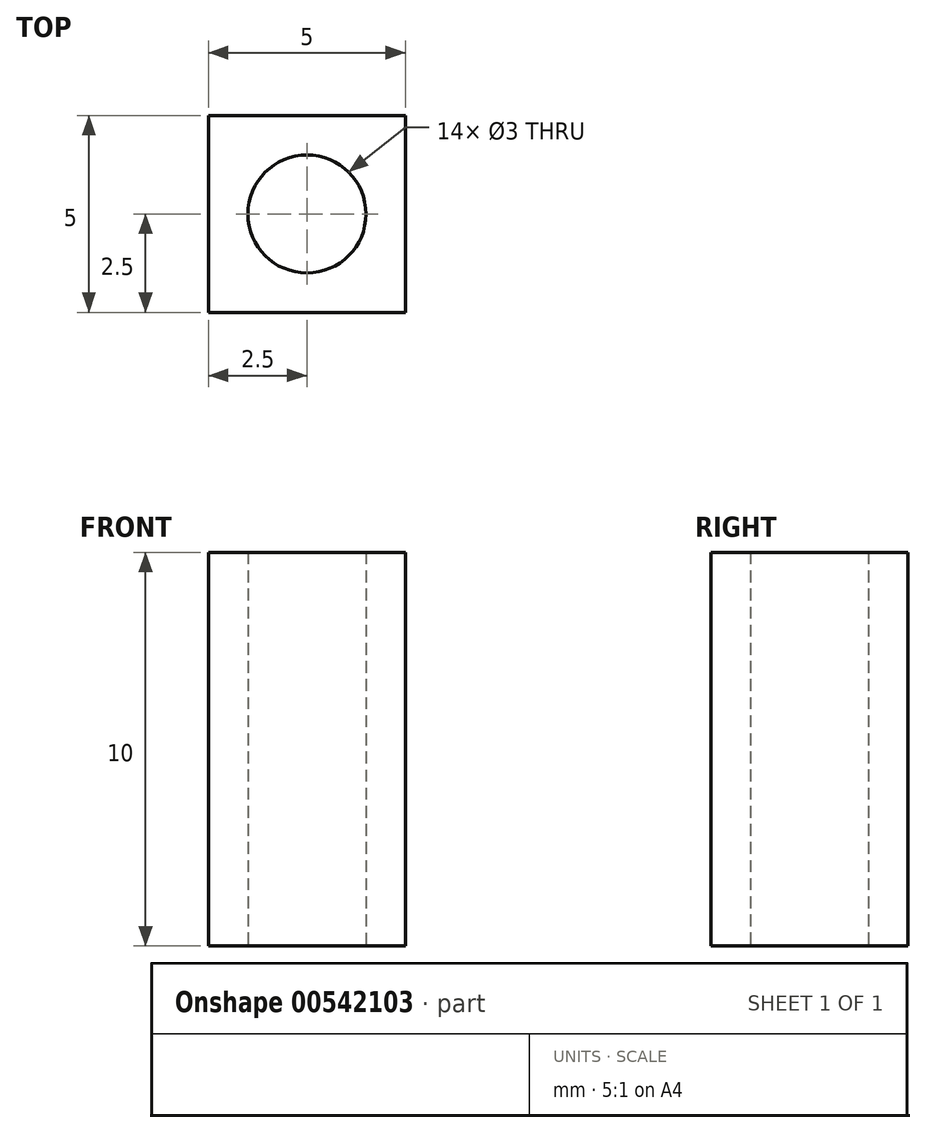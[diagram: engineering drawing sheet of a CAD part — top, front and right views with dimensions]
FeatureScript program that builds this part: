
annotation { "Feature Type Name" : "Feature", "Feature Type Description" : "" }
export const myFeature = defineFeature(function(context is Context, id is Id, definition is map)
    precondition{}
    {
        {
            var Q0;
            Q0=qCreatedBy(makeId("Top.planeOp"),FACE);
            var sketch = newSketch(context, id + "F0", { "sketchPlane" : qUnion([Q0])});
            skLineSegment(sketch, "E0.bottom", {"start": v(2.5, -2.5) * mm, "end": v(-2.5, -2.5) * mm});
            skLineSegment(sketch, "E0.top", {"start": v(2.5, 2.5) * mm, "end": v(-2.5, 2.5) * mm});
            skLineSegment(sketch, "E0.left", {"start": v(2.5, -2.5) * mm, "end": v(2.5, 2.5) * mm});
            skLineSegment(sketch, "E0.right", {"start": v(-2.5, -2.5) * mm, "end": v(-2.5, 2.5) * mm});
            skPoint(sketch, "E0.middle", {"position": v(0, 0) * mm});
            skPoint(sketch, "E1.0.midPoint", {"position": v(0, 3.25) * mm});
            skCircle(sketch, "E2", {"center": v(0, 0) * mm, "radius": 1.5 * mm});
            skLineSegment(sketch, "E3", {"start": v(-2.5, 2.5) * mm, "end": v(2.5, 2.5) * mm});
            skSolve(sketch);
        }
        {
            var Q0;
            Q0=makeQuery(id+"F0.imprint","IMPRINT",FACE,{"disambiguationData":[TD([[makeQuery(id+"F0.imprint","IMPRINT",EDGE,{"derivedFrom":sQuery(id+"F0.wireOp",EDGE,"E0.bottom")}),-1.0]])]});
            extrude(context, id + "F1", {"entities" : qUnion([Q0]), "depth" : 10 * mm, "offsetDistance" : 25 * mm});
        }
    });
